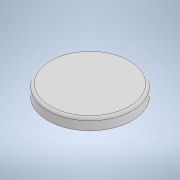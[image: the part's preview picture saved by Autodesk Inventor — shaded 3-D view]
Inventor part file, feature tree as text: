
AUTODESK INVENTOR PART (.ipt)
format: ipt  version: 2022 (Build 260153000, 153)  size: 142,848 bytes
history: native  units: in
note: dims shown in document units (in); Inventor stores cm internally (conversion verified against a paired STEP export)
features: sketch x2, revolve x1, fillet x1, extrude x1
ambient origin geometry x8: Origin, YZ Plane, XZ Plane, XY Plane, X Axis, Y Axis, Z Axis, Center Point
bodies: Solid1 (feature_tree)
feature tree (5):
  revolve  "Revolution1"  [1 undecoded]
  fillet  "Fillet1"  Radius=0.2362in
  extrude  "Extrusion1"  Depth=0.1575in
  sketch  "Sketch2"  dims[d0=1.9114in d1=0.1575in d2=0.2362in]
  sketch  "Sketch3"  dims[d3=0.5118in d4=0.1575in d5=0.2756in d6=90.0deg d7=0.1181in d8=1.3386in d9=0.7874in d11=360.0deg d13=0.1969in d14=0.0in d15=0.7697in]
note: 1 required parameter value undecoded (feature->parameter linkage not recoverable at this tier; creation-order binding heuristic only, values carry confidence <= 0.55)
